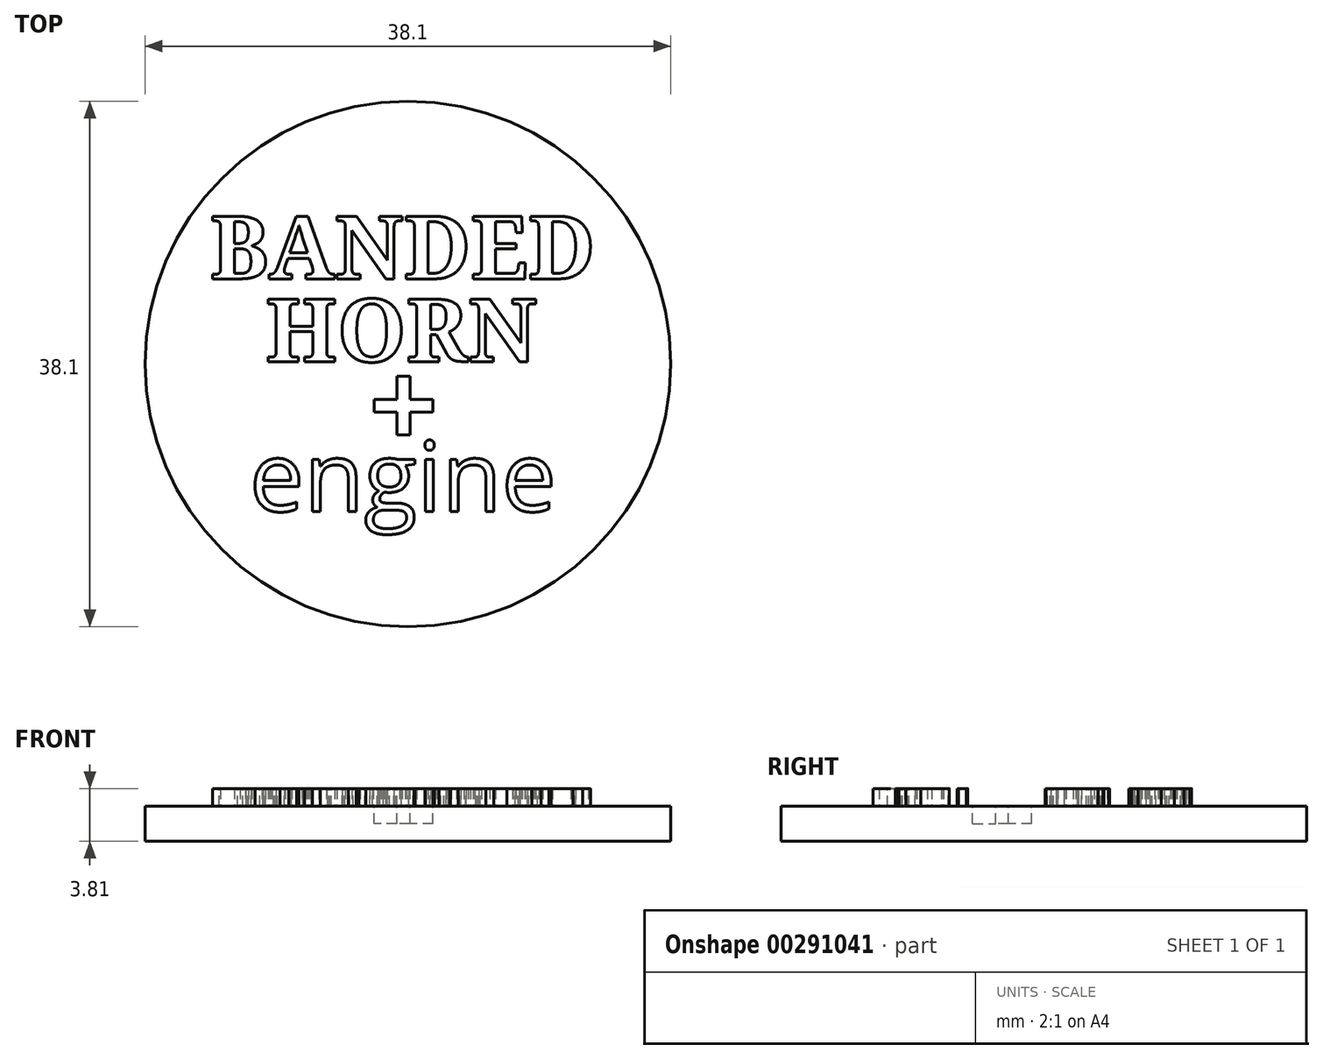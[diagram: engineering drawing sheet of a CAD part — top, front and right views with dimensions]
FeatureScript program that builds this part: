
annotation { "Feature Type Name" : "Feature", "Feature Type Description" : "" }
export const myFeature = defineFeature(function(context is Context, id is Id, definition is map)
    precondition{}
    {
        {
            var Q0;
            Q0=qCreatedBy(makeId("Top.planeOp"),FACE);
            var sketch = newSketch(context, id + "F0", { "sketchPlane" : qUnion([Q0])});
            skCircle(sketch, "E0", {"center": v(0, 0) * mm, "radius": 19.05 * mm});
            skSolve(sketch);
        }
        {
            var Q0;
            Q0 = qSketchRegion(id + "F0", true);
            extrude(context, id + "F1", {"entities" : qUnion([Q0]), "depth" : 2.54 * mm});
        }
        {
            var Q0;
            Q0=makeQuery(id+"F1.opExtrude","CAP_FACE",FACE,{"disambiguationData":[OSD([sQuery(id+"F0.wireOp",EDGE,"E0")])],"isStart":false});
            var sketch = newSketch(context, id + "F2", { "sketchPlane" : qUnion([Q0])});
            skText(sketch, "E1", { "text": "HORN", "fontName": "NotoSerif-Bold.ttf"});
            skText(sketch, "E2", { "text": "engine", "fontName": "OpenSans-Regular.ttf"});
            skText(sketch, "E3", { "text": "BANDED", "fontName": "NotoSerif-Bold.ttf"});
            const initialGuessF2  = {"E1": [-0.01032, 0.00016, 1, 0, 0.00457], "E2": [-0.01148, -0.01069, 1, 0, 0.00508], "E3": [-0.01435, 0.00617, 1, 0, 0.00457]};
            skSetInitialGuess(sketch, initialGuessF2);
            skSolve(sketch);
        }
        {
            var Q0;
            Q0 = qSketchRegion(id + "F2", true);
            extrude(context, id + "F3", {"entities" : qUnion([Q0]), "operationType" : NewBodyOperationType.ADD, "depth" : 1.27 * mm});
        }
        {
            var Q0;
            Q0=makeQuery(id+"F1.opExtrude","CAP_FACE",FACE,{"disambiguationData":[OSD([sQuery(id+"F0.wireOp",EDGE,"E0")])],"isStart":false});
            var sketch = newSketch(context, id + "F4", { "sketchPlane" : qUnion([Q0])});
            skText(sketch, "E4", { "text": "+", "fontName": "OpenSans-Bold.ttf"});
            const initialGuessF4  = {"E4": [-0.00284, -0.00614, 1, 0, 0.00635]};
            skSetInitialGuess(sketch, initialGuessF4);
            skSolve(sketch);
        }
        {
            var Q0;
            Q0 = qSketchRegion(id + "F4", true);
            extrude(context, id + "F5", {"entities" : qUnion([Q0]), "operationType" : NewBodyOperationType.REMOVE, "oppositeDirection" : true, "depth" : 1.27 * mm});
        }
    });
